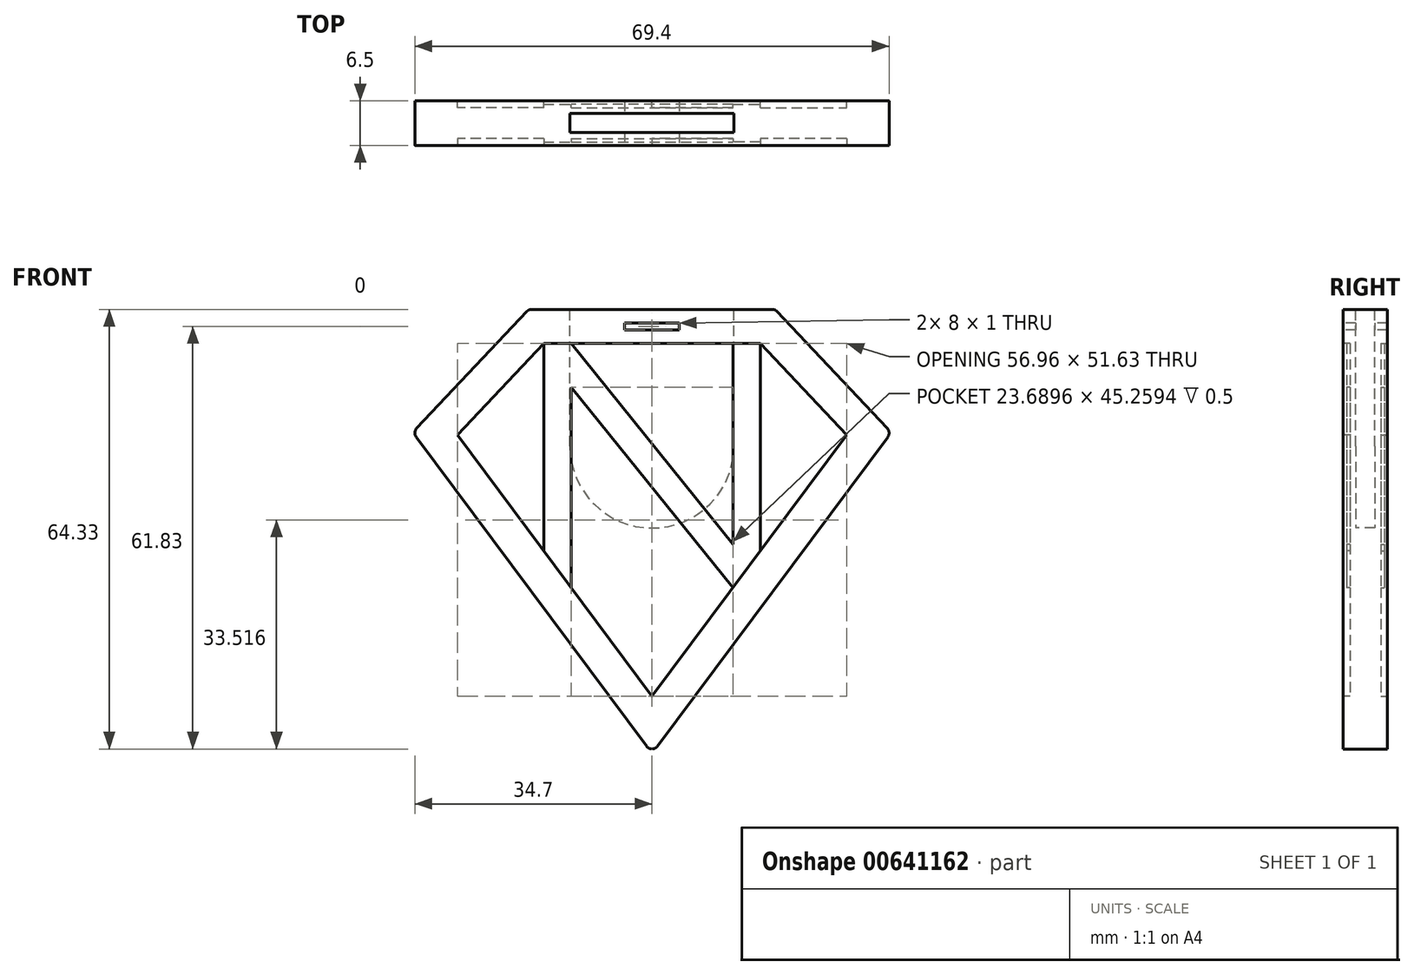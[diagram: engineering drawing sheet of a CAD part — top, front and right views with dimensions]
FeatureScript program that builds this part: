
annotation { "Feature Type Name" : "Feature", "Feature Type Description" : "" }
export const myFeature = defineFeature(function(context is Context, id is Id, definition is map)
    precondition{}
    {
        {
            var Q0;
            Q0=qCreatedBy(makeId("Front.planeOp"),FACE);
            var sketch = newSketch(context, id + "F0", { "sketchPlane" : qUnion([Q0])});
            skLineSegment(sketch, "E0", {"start": v(0, 18) * mm, "end": v(18, 18) * mm});
            skLineSegment(sketch, "E1", {"start": v(18, 18) * mm, "end": v(35, 0) * mm});
            skLineSegment(sketch, "E2", {"start": v(35, 0) * mm, "end": v(0, -47) * mm});
            skLineSegment(sketch, "E3", {"start": v(0, 18) * mm, "end": v(0, -47) * mm, "construction": true});
            skLineSegment(sketch, "E4.MirrorCS", {"start": v(-35, 0) * mm, "end": v(0, -47) * mm});
            skLineSegment(sketch, "E5.MirrorCS", {"start": v(-18, 18) * mm, "end": v(-35, 0) * mm});
            skLineSegment(sketch, "E6.MirrorCS", {"start": v(0, 18) * mm, "end": v(-18, 18) * mm});
            skSolve(sketch);
        }
        {
            var Q0;
            Q0=qSketchRegion(id+"F0",true);
            extrude(context, id + "F1", {"entities" : qUnion([Q0]), "endBound" : BoundingType.SYMMETRIC, "depth" : 6.5 * mm, "offsetDistance" : 25 * mm});
        }
        {
            var Q0;
            Q0=makeQuery(id+"F1.opExtrude","CAP_FACE",FACE,{"disambiguationData":[OSD([sQuery(id+"F0.wireOp",EDGE,"E0"),sQuery(id+"F0.wireOp",EDGE,"E1"),sQuery(id+"F0.wireOp",EDGE,"E2"),sQuery(id+"F0.wireOp",EDGE,"E4.MirrorCS"),sQuery(id+"F0.wireOp",EDGE,"E5.MirrorCS"),sQuery(id+"F0.wireOp",EDGE,"E6.MirrorCS")])],"isStart":false});
            var sketch = newSketch(context, id + "F2", { "sketchPlane" : qUnion([Q0])});
            skLineSegment(sketch, "E7.0", {"start": v(-15.84, 13) * mm, "end": v(15.84, 13) * mm});
            skLineSegment(sketch, "E8.0", {"start": v(-15.84, 13) * mm, "end": v(-28.48, -0.38) * mm});
            skLineSegment(sketch, "E9.0", {"start": v(-28.48, -0.38) * mm, "end": v(0, -38.63) * mm});
            skLineSegment(sketch, "E10.0", {"start": v(28.48, -0.38) * mm, "end": v(0, -38.63) * mm});
            skLineSegment(sketch, "E11.0", {"start": v(15.84, 13) * mm, "end": v(28.48, -0.38) * mm});
            skSolve(sketch);
        }
        {
            var Q0;
            Q0=qSketchRegion(id+"F2",true);
            extrude(context, id + "F3", {"entities" : qUnion([Q0]), "operationType" : NewBodyOperationType.REMOVE, "oppositeDirection" : true, "depth" : 0.5 * mm, "offsetDistance" : 25 * mm});
        }
        {
            var Q0;
            Q0=makeQuery(id+"F1.opExtrude","CAP_FACE",FACE,{"disambiguationData":[OSD([sQuery(id+"F0.wireOp",EDGE,"E0"),sQuery(id+"F0.wireOp",EDGE,"E1"),sQuery(id+"F0.wireOp",EDGE,"E2"),sQuery(id+"F0.wireOp",EDGE,"E4.MirrorCS"),sQuery(id+"F0.wireOp",EDGE,"E5.MirrorCS"),sQuery(id+"F0.wireOp",EDGE,"E6.MirrorCS")])],"isStart":true});
            var sketch = newSketch(context, id + "F4", { "sketchPlane" : qUnion([Q0])});
            skLineSegment(sketch, "E12.0", {"start": v(15.84, 13) * mm, "end": v(-15.84, 13) * mm});
            skLineSegment(sketch, "E13.0", {"start": v(15.84, 13) * mm, "end": v(28.48, -0.38) * mm});
            skLineSegment(sketch, "E14.0", {"start": v(28.48, -0.38) * mm, "end": v(0, -38.63) * mm});
            skLineSegment(sketch, "E15.0", {"start": v(-28.48, -0.38) * mm, "end": v(0, -38.63) * mm});
            skLineSegment(sketch, "E15.1", {"start": v(-15.84, 13) * mm, "end": v(-28.48, -0.38) * mm});
            skSolve(sketch);
        }
        {
            var Q0;
            Q0=qSketchRegion(id+"F4",true);
            extrude(context, id + "F5", {"entities" : qUnion([Q0]), "operationType" : NewBodyOperationType.REMOVE, "oppositeDirection" : true, "depth" : 0.5 * mm, "offsetDistance" : 25 * mm});
        }
        {
            var Q0;
            Q0=makeQuery(id+"F3.boolean.opBoolean","COPY",FACE,{"derivedFrom":makeQuery(id+"F3.opExtrude","CAP_FACE",FACE,{"disambiguationData":[OSD([sQuery(id+"F2.wireOp",EDGE,"E7.0"),sQuery(id+"F2.wireOp",EDGE,"E8.0"),sQuery(id+"F2.wireOp",EDGE,"E9.0"),sQuery(id+"F2.wireOp",EDGE,"E10.0"),sQuery(id+"F2.wireOp",EDGE,"E11.0")])],"isStart":false})});
            var sketch = newSketch(context, id + "F6", { "sketchPlane" : qUnion([Q0])});
            skLineSegment(sketch, "E16", {"start": v(-15.84, 13) * mm, "end": v(-15.84, -17.35) * mm});
            skLineSegment(sketch, "E17", {"start": v(15.84, 13) * mm, "end": v(15.84, -17.35) * mm});
            skLineSegment(sketch, "E18.0", {"start": v(-11.84, 6.63) * mm, "end": v(-11.84, -22.72) * mm});
            skLineSegment(sketch, "E19.0", {"start": v(11.84, 13) * mm, "end": v(11.84, -16.35) * mm});
            skLineSegment(sketch, "E20.0", {"start": v(-11.84, 6.63) * mm, "end": v(11.84, -22.72) * mm});
            skPoint(sketch, "E21.0.start.orphan", {"position": v(-15.84, 13) * mm});
            skLineSegment(sketch, "E22", {"start": v(-11.84, 13) * mm, "end": v(11.84, 13) * mm});
            skLineSegment(sketch, "E23", {"start": v(-15.84, 13) * mm, "end": v(-28.48, -0.38) * mm});
            skLineSegment(sketch, "E24", {"start": v(-28.48, -0.38) * mm, "end": v(-15.84, -17.35) * mm});
            skLineSegment(sketch, "E25", {"start": v(0, -38.63) * mm, "end": v(11.84, -22.72) * mm});
            skLineSegment(sketch, "E26", {"start": v(28.48, -0.38) * mm, "end": v(15.84, 13) * mm});
            skLineSegment(sketch, "E27.trimOffspring", {"start": v(15.84, -17.35) * mm, "end": v(28.48, -0.38) * mm});
            skLineSegment(sketch, "E28.trimOffspring", {"start": v(-11.84, -22.72) * mm, "end": v(0, -38.63) * mm});
            skLineSegment(sketch, "E29.0", {"start": v(-11.84, 13) * mm, "end": v(11.84, -16.35) * mm});
            skSolve(sketch);
        }
        {
            var Q0;
            Q0=qSketchRegion(id+"F6",true);
            extrude(context, id + "F7", {"entities" : qUnion([Q0]), "operationType" : NewBodyOperationType.REMOVE, "oppositeDirection" : true, "depth" : 0.5 * mm, "offsetDistance" : 25 * mm});
        }
        {
            var Q0;
            Q0=makeQuery(id+"F5.boolean.opBoolean","COPY",FACE,{"derivedFrom":makeQuery(id+"F5.opExtrude","CAP_FACE",FACE,{"disambiguationData":[OSD([sQuery(id+"F4.wireOp",EDGE,"E12.0"),sQuery(id+"F4.wireOp",EDGE,"E13.0"),sQuery(id+"F4.wireOp",EDGE,"E14.0"),sQuery(id+"F4.wireOp",EDGE,"E15.0"),sQuery(id+"F4.wireOp",EDGE,"E15.1")])],"isStart":false})});
            var sketch = newSketch(context, id + "F8", { "sketchPlane" : qUnion([Q0])});
            skLineSegment(sketch, "E30.0", {"start": v(-15.84, 13) * mm, "end": v(-15.84, -17.35) * mm});
            skLineSegment(sketch, "E30.7", {"start": v(15.84, 13) * mm, "end": v(15.84, -17.35) * mm});
            skLineSegment(sketch, "E30.8", {"start": v(15.84, 13) * mm, "end": v(28.48, -0.38) * mm});
            skLineSegment(sketch, "E30.9", {"start": v(28.48, -0.38) * mm, "end": v(15.84, -17.35) * mm});
            skLineSegment(sketch, "E30.10", {"start": v(-28.48, -0.38) * mm, "end": v(-15.84, -17.35) * mm});
            skLineSegment(sketch, "E30.11", {"start": v(-15.84, 13) * mm, "end": v(-28.48, -0.38) * mm});
            skLineSegment(sketch, "E30.12", {"start": v(11.84, 13) * mm, "end": v(-11.84, 13) * mm});
            skLineSegment(sketch, "E31.trimOffspring", {"start": v(11.84, -22.72) * mm, "end": v(0, -38.63) * mm});
            skLineSegment(sketch, "E32", {"start": v(-11.84, 13) * mm, "end": v(11.84, -16.35) * mm});
            skLineSegment(sketch, "E33.0", {"start": v(-11.84, 6.63) * mm, "end": v(-11.84, -22.72) * mm});
            skLineSegment(sketch, "E34.0", {"start": v(-11.84, 6.63) * mm, "end": v(11.84, -22.72) * mm});
            skLineSegment(sketch, "E35", {"start": v(11.84, 13) * mm, "end": v(11.84, -16.35) * mm});
            skLineSegment(sketch, "E36", {"start": v(0, -38.63) * mm, "end": v(-11.84, -22.72) * mm});
            skSolve(sketch);
        }
        {
            var Q0;
            Q0=qSketchRegion(id+"F8",true);
            extrude(context, id + "F9", {"entities" : qUnion([Q0]), "operationType" : NewBodyOperationType.REMOVE, "oppositeDirection" : true, "depth" : 0.5 * mm, "offsetDistance" : 25 * mm});
        }
        {
            var Q0;
            Q0=makeQuery(id+"F1.opExtrude","SWEPT_FACE",FACE,{"disambiguationData":[OSD([sQuery(id+"F0.wireOp",EDGE,"E0"),sQuery(id+"F0.wireOp",EDGE,"E6.MirrorCS")])]});
            var sketch = newSketch(context, id + "F10", { "sketchPlane" : qUnion([Q0])});
            skLineSegment(sketch, "E37.bottom", {"start": v(-12, 1.4) * mm, "end": v(12, 1.4) * mm});
            skLineSegment(sketch, "E37.top", {"start": v(-12, -1.4) * mm, "end": v(12, -1.4) * mm});
            skLineSegment(sketch, "E37.left", {"start": v(-12, 1.4) * mm, "end": v(-12, -1.4) * mm});
            skLineSegment(sketch, "E37.right", {"start": v(12, 1.4) * mm, "end": v(12, -1.4) * mm});
            skSolve(sketch);
        }
        {
            var Q0;
            Q0=qSketchRegion(id+"F10",true);
            extrude(context, id + "F11", {"entities" : qUnion([Q0]), "operationType" : NewBodyOperationType.REMOVE, "oppositeDirection" : true, "depth" : 20 * mm, "offsetDistance" : 25 * mm});
        }
        {
            var Q0;
            Q0=qCreatedBy(makeId("Front.planeOp"),FACE);
            var sketch = newSketch(context, id + "F12", { "sketchPlane" : qUnion([Q0])});
            skLineSegment(sketch, "E38.0", {"start": v(-12, -2) * mm, "end": v(12, -2) * mm});
            skArc(sketch, "E39", {"start": v(-12, -2) * mm, "mid": v(0, -14) * mm, "end": v(12, -2) * mm});
            skSolve(sketch);
        }
        {
            var Q0;
            Q0=qSketchRegion(id+"F12",true);
            extrude(context, id + "F13", {"entities" : qUnion([Q0]), "operationType" : NewBodyOperationType.REMOVE, "endBound" : BoundingType.SYMMETRIC, "oppositeDirection" : true, "depth" : 2.8 * mm, "offsetDistance" : 25 * mm});
        }
        {
            var Q0;
            Q0=makeQuery(id+"F1.opExtrude","CAP_FACE",FACE,{"disambiguationData":[OSD([sQuery(id+"F0.wireOp",EDGE,"E0"),sQuery(id+"F0.wireOp",EDGE,"E1"),sQuery(id+"F0.wireOp",EDGE,"E2"),sQuery(id+"F0.wireOp",EDGE,"E4.MirrorCS"),sQuery(id+"F0.wireOp",EDGE,"E5.MirrorCS"),sQuery(id+"F0.wireOp",EDGE,"E6.MirrorCS")])],"isStart":false});
            var sketch = newSketch(context, id + "F14", { "sketchPlane" : qUnion([Q0])});
            skLineSegment(sketch, "E40.bottom", {"start": v(-4, 16) * mm, "end": v(4, 16) * mm});
            skLineSegment(sketch, "E40.top", {"start": v(-4, 15) * mm, "end": v(4, 15) * mm});
            skLineSegment(sketch, "E40.left", {"start": v(-4, 16) * mm, "end": v(-4, 15) * mm});
            skLineSegment(sketch, "E40.right", {"start": v(4, 16) * mm, "end": v(4, 15) * mm});
            skSolve(sketch);
        }
        {
            var Q0;
            Q0=qSketchRegion(id+"F14",true);
            extrude(context, id + "F15", {"entities" : qUnion([Q0]), "operationType" : NewBodyOperationType.REMOVE, "oppositeDirection" : true, "depth" : 25 * mm, "offsetDistance" : 25 * mm});
        }
        {
            var Q0;
            Q0=makeQuery(id+"F1.opExtrude","SWEPT_EDGE",EDGE,{"disambiguationData":[OSD([sQuery(id+"F0.wireOp",EDGE,"E2"),sQuery(id+"F0.wireOp",EDGE,"E4.MirrorCS")])]});
            var Q1;
            Q1=makeQuery(id+"F1.opExtrude","SWEPT_EDGE",EDGE,{"disambiguationData":[OSD([sQuery(id+"F0.wireOp",EDGE,"E1"),sQuery(id+"F0.wireOp",EDGE,"E2")])]});
            var Q2;
            Q2=makeQuery(id+"F1.opExtrude","SWEPT_EDGE",EDGE,{"disambiguationData":[OSD([sQuery(id+"F0.wireOp",EDGE,"E4.MirrorCS"),sQuery(id+"F0.wireOp",EDGE,"E5.MirrorCS")])]});
            var Q3;
            Q3=makeQuery(id+"F1.opExtrude","SWEPT_EDGE",EDGE,{"disambiguationData":[OSD([sQuery(id+"F0.wireOp",EDGE,"E5.MirrorCS"),sQuery(id+"F0.wireOp",EDGE,"E6.MirrorCS")])]});
            var Q4;
            Q4=makeQuery(id+"F1.opExtrude","SWEPT_EDGE",EDGE,{"disambiguationData":[OSD([sQuery(id+"F0.wireOp",EDGE,"E0"),sQuery(id+"F0.wireOp",EDGE,"E1")])]});
            fillet(context, id + "F16", {"entities" : qUnion([Q0, Q1, Q2, Q3, Q4]), "radius" : 1 * mm, "tangentPropagation" : true, "allowEdgeOverflow" : false});
        }
    });
